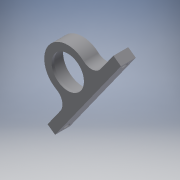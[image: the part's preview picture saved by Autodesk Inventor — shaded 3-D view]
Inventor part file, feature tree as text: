
AUTODESK INVENTOR PART (.ipt)
format: ipt  version: 2017 (Build 210142000, 142)  size: 144,896 bytes
history: native  units: in
note: dims shown in document units (in); Inventor stores cm internally (conversion verified against a paired STEP export)
features: other x4, extrude x3, sketch x3, reference x3, projected_geometry x2
ambient origin geometry x8: Origin, YZ Plane, XZ Plane, XY Plane, X Axis, Y Axis, Z Axis, Center Point
bodies: Solid1 (feature_tree)
feature tree (15):
  extrude  "Extrusion1"  Depth=0.3346in TaperAngle=0.0deg
  extrude  "Extrusion2"  Depth=0.0591in TaperAngle=0.0deg
  extrude  "Extrusion3"  Depth=2.5591in
  sketch  "Sketch1"  dims[d0=0.0984in d1=0.3346in d2=0.0in]
  reference  "Reference1"
  reference  "Reference2"
  sketch  "Sketch2"  dims[d3=0.7309in d4=0.0591in d5=0.0in]
  reference  "Reference3"
  sketch  "Sketch3"  dims[d8=0.0591in d9=0.0in d10=0.1378in d11=0.1378in d12=2.5591in d13=0.1575in d14=0.1575in d15=0.8858in]
  projected_geometry  "Projected Loop1"
  projected_geometry  "Projected Loop2"
  other  "Rubiks Arm Assembly.iam"
  other  "8mmx22mm bearing:1"
  other  "Base Plate:1"
  other  "coupler:1"
